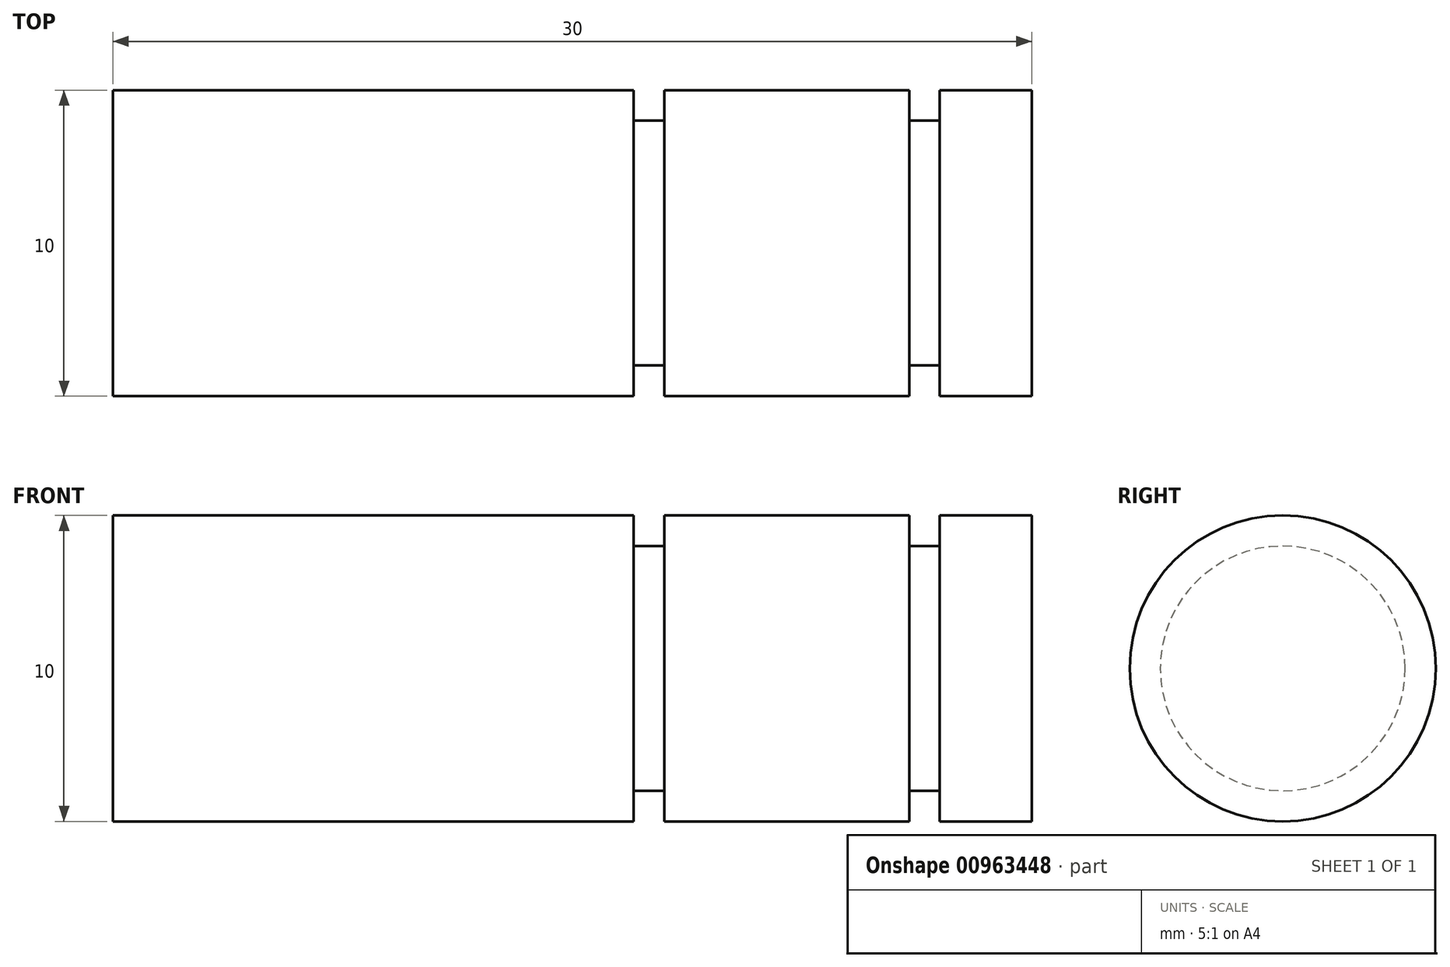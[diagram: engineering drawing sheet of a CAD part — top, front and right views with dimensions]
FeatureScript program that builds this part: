
annotation { "Feature Type Name" : "Feature", "Feature Type Description" : "" }
export const myFeature = defineFeature(function(context is Context, id is Id, definition is map)
    precondition{}
    {
        {
            var Q0;
            Q0=qCreatedBy(makeId("Front.planeOp"),FACE);
            var sketch = newSketch(context, id + "F0", { "sketchPlane" : qUnion([Q0])});
            skLineSegment(sketch, "E0", {"start": v(0, 0) * mm, "end": v(0, 5) * mm});
            skLineSegment(sketch, "E1", {"start": v(0, 5) * mm, "end": v(17, 5) * mm});
            skLineSegment(sketch, "E2", {"start": v(30, 5) * mm, "end": v(30, 0) * mm});
            skLineSegment(sketch, "E3", {"start": v(30, 0) * mm, "end": v(0, 0) * mm});
            skLineSegment(sketch, "E4.top", {"start": v(17, 4) * mm, "end": v(18, 4) * mm});
            skLineSegment(sketch, "E4.left", {"start": v(17, 5) * mm, "end": v(17, 4) * mm});
            skLineSegment(sketch, "E4.right", {"start": v(18, 5) * mm, "end": v(18, 4) * mm});
            skLineSegment(sketch, "E5.top", {"start": v(26, 4) * mm, "end": v(27, 4) * mm});
            skLineSegment(sketch, "E5.left", {"start": v(26, 5) * mm, "end": v(26, 4) * mm});
            skLineSegment(sketch, "E5.right", {"start": v(27, 5) * mm, "end": v(27, 4) * mm});
            skLineSegment(sketch, "E6.trimOffspring", {"start": v(18, 5) * mm, "end": v(26, 5) * mm});
            skLineSegment(sketch, "E7.trimOffspring", {"start": v(27, 5) * mm, "end": v(30, 5) * mm});
            skLineSegment(sketch, "E8", {"start": v(-15.37, 0) * mm, "end": v(44.9, 0) * mm, "construction": true});
            skSolve(sketch);
        }
        {
            var Q0;
            Q0=qSketchRegion(id+"F0",true);
            var Q1;
            Q1=sQuery(id+"F0.wireOp",EDGE,"E8");
            revolve(context, id + "F1", {"entities" : qUnion([Q0]), "axis" : qUnion([Q1]), "revolveType" : RevolveType.FULL});
        }
    });
